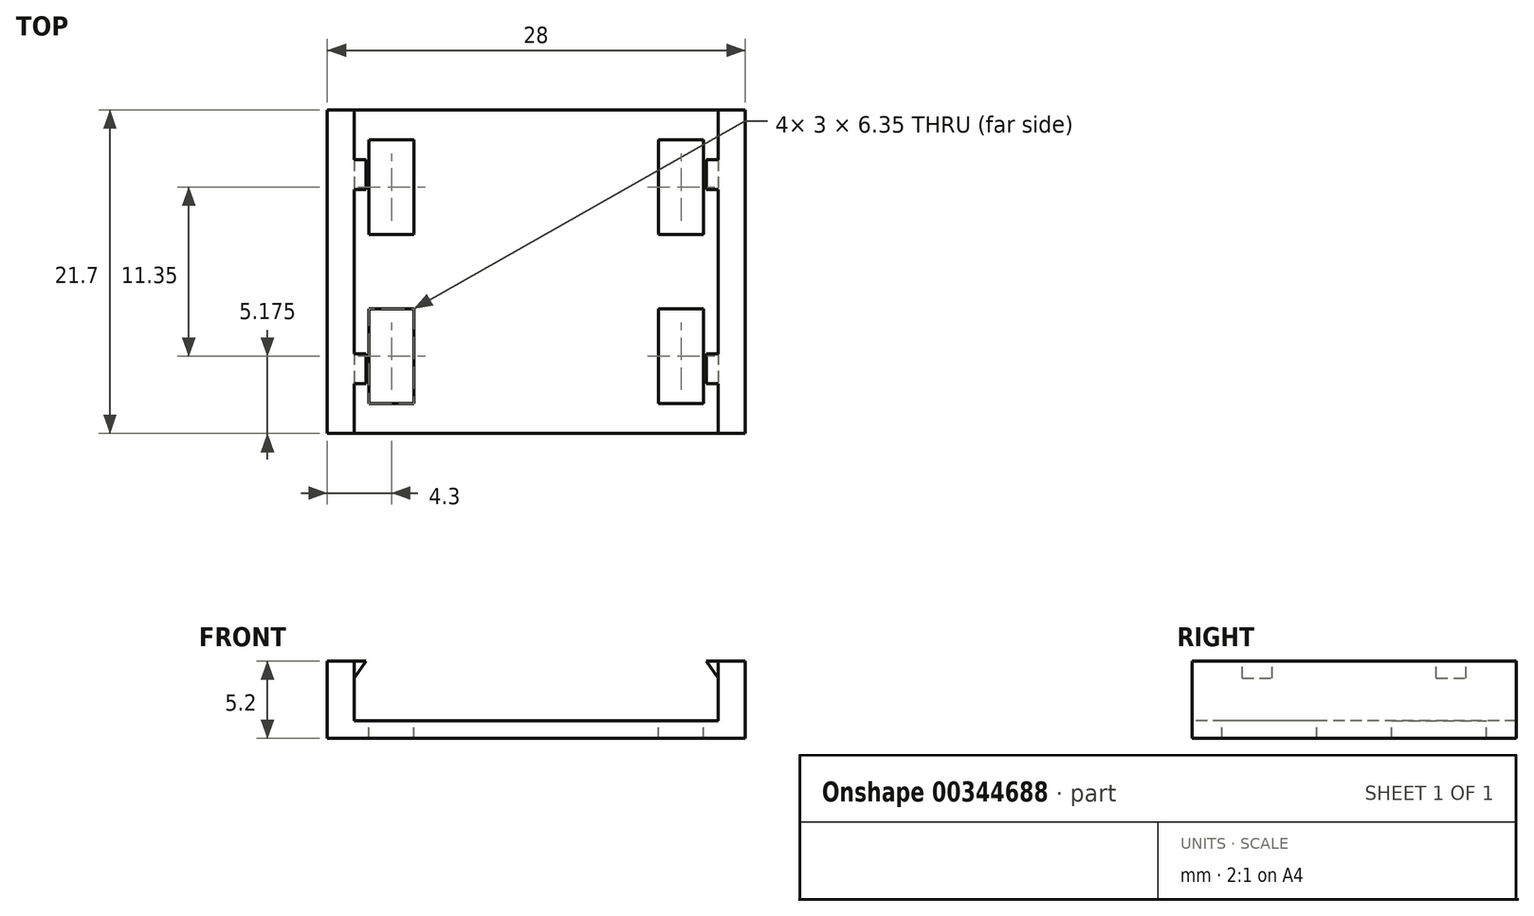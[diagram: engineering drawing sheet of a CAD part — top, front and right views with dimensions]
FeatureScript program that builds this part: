
annotation { "Feature Type Name" : "Feature", "Feature Type Description" : "" }
export const myFeature = defineFeature(function(context is Context, id is Id, definition is map)
    precondition{}
    {
        {
            var Q0;
            Q0=qCreatedBy(makeId("Top.planeOp"),FACE);
            var sketch = newSketch(context, id + "F0", { "sketchPlane" : qUnion([Q0])});
            skLineSegment(sketch, "E0.bottom", {"start": v(-14, 16.35) * mm, "end": v(14, 16.35) * mm});
            skLineSegment(sketch, "E0.top", {"start": v(-14, -16.35) * mm, "end": v(14, -16.35) * mm});
            skLineSegment(sketch, "E0.left", {"start": v(-14, 16.35) * mm, "end": v(-14, -16.35) * mm});
            skLineSegment(sketch, "E0.right", {"start": v(14, 16.35) * mm, "end": v(14, -16.35) * mm});
            skPoint(sketch, "E0.middle", {"position": v(0, 0) * mm});
            skSolve(sketch);
        }
        {
            var Q0;
            Q0=makeQuery(id+"F0.imprint","IMPRINT",FACE,{"disambiguationData":[TD([[makeQuery(id+"F0.imprint","IMPRINT",EDGE,{"derivedFrom":sQuery(id+"F0.wireOp",EDGE,"E0.bottom")}),-1.0]])]});
            extrude(context, id + "F1", {"entities" : qUnion([Q0]), "depth" : 1.2 * mm});
        }
        {
            var Q0;
            {var subQ5=sQuery(id+"F0.wireOp",EDGE,"E0.right");var subQ6=sQuery(id+"F0.wireOp",EDGE,"E0.left");var subQ7=sQuery(id+"F0.wireOp",EDGE,"E0.top");var subQ8=sQuery(id+"F0.wireOp",EDGE,"E0.bottom");var subQ9=makeQuery(id+"F1.opExtrude","CAP_FACE",FACE,{"disambiguationData":[OSD([subQ8,subQ7,subQ6,subQ5])],"isStart":false});var subQ12=subQ9;Q0=makeQuery(id+"FTskU3KK5imesQs_1.opFillet","MERGE",FACE,{"derivedFrom":[makeQuery(id+"FZi3CJKkktuihJ1_1.boolean.opBoolean","SPLIT",FACE,{"disambiguationData":[TD([makeQuery(id+"F1.opExtrude","SWEPT_FACE",FACE,{"disambiguationData":[OSD([subQ8])]})])],"derivedFrom":subQ12}),makeQuery(id+"FZ7EBSF1tdb4njM_1.boolean.opBoolean","MERGE",FACE,{"derivedFrom":[makeQuery(id+"FZi3CJKkktuihJ1_1.boolean.opBoolean","SPLIT",FACE,{"disambiguationData":[TD([makeQuery(id+"FlsG0jWeIkAughT_1.opExtrude","SWEPT_FACE",FACE,{"disambiguationData":[OSD([sQuery(id+"F5Wyuop6bpOGen8_1.wireOp",EDGE,"vaNtV44L-idVL-UOBQ-HHhe-vYpkaX2QMto8.bottom")])]})])],"derivedFrom":subQ12}),makeQuery(id+"FZ7EBSF1tdb4njM_1.opExtrude","CAP_FACE",FACE,{"disambiguationData":[OSD([sQuery(id+"FoSm93bD1NxVTFu_1.wireOp",EDGE,"97a7e462-43fe-4127-a601-1d90c2ab95a00.MirrorCS"),sQuery(id+"FoSm93bD1NxVTFu_1.wireOp",EDGE,"97a7e462-43fe-4127-a601-1d90c2ab95a01.MirrorCS"),sQuery(id+"FoSm93bD1NxVTFu_1.wireOp",EDGE,"97a7e462-43fe-4127-a601-1d90c2ab95a02.MirrorCS"),sQuery(id+"FoSm93bD1NxVTFu_1.wireOp",EDGE,"97a7e462-43fe-4127-a601-1d90c2ab95a03.MirrorCS")])],"isStart":false})]}),makeQuery(id+"FZ7EBSF1tdb4njM_1.boolean.opBoolean","MERGE",FACE,{"derivedFrom":[makeQuery(id+"FZi3CJKkktuihJ1_1.boolean.opBoolean","SPLIT",FACE,{"disambiguationData":[TD([makeQuery(id+"FlsG0jWeIkAughT_1.opExtrude","SWEPT_FACE",FACE,{"disambiguationData":[OSD([sQuery(id+"F5Wyuop6bpOGen8_1.wireOp",EDGE,"5b2c8ccd-c1e1-48dd-aecc-73c440124aab0.MirrorCS")])]})])],"derivedFrom":subQ12}),makeQuery(id+"FZ7EBSF1tdb4njM_1.opExtrude","CAP_FACE",FACE,{"disambiguationData":[OSD([sQuery(id+"FoSm93bD1NxVTFu_1.wireOp",EDGE,"85c03d27-702a-4580-8be8-e1d3315b53173.MirrorCS"),sQuery(id+"FoSm93bD1NxVTFu_1.wireOp",EDGE,"85c03d27-702a-4580-8be8-e1d3315b53174.MirrorCS"),sQuery(id+"FoSm93bD1NxVTFu_1.wireOp",EDGE,"85c03d27-702a-4580-8be8-e1d3315b53176.MirrorCS"),sQuery(id+"FoSm93bD1NxVTFu_1.wireOp",EDGE,"85c03d27-702a-4580-8be8-e1d3315b53177.MirrorCS")])],"isStart":false})]})]});}
            var sketch = newSketch(context, id + "F2", { "sketchPlane" : qUnion([Q0])});
            skLineSegment(sketch, "E1.bottom", {"start": v(-12.2, 15.35) * mm, "end": v(12.2, 15.35) * mm});
            skLineSegment(sketch, "E1.top", {"start": v(-12.2, -15.35) * mm, "end": v(12.2, -15.35) * mm});
            skLineSegment(sketch, "E1.left", {"start": v(-12.2, 15.35) * mm, "end": v(-12.2, -15.35) * mm});
            skLineSegment(sketch, "E1.right", {"start": v(12.2, 15.35) * mm, "end": v(12.2, -15.35) * mm});
            skPoint(sketch, "E1.middle", {"position": v(0, 0) * mm});
            skSolve(sketch);
        }
        {
            var Q0;
            Q0=makeQuery(id+"F2.imprint","IMPRINT",FACE,{"disambiguationData":[TD([[makeQuery(id+"F2.imprint","IMPRINT",EDGE,{"derivedFrom":sQuery(id+"F2.wireOp",EDGE,"E1.bottom")}),1.0]])]});
            extrude(context, id + "F3", {"entities" : qUnion([Q0]), "operationType" : NewBodyOperationType.ADD, "depth" : 4 * mm});
        }
        {
            var Q0;
            Q0=makeQuery(id+"F3.opExtrude","CAP_FACE",FACE,{"disambiguationData":[OSD([sQuery(id+"F0.wireOp",EDGE,"E0.bottom"),sQuery(id+"F0.wireOp",EDGE,"E0.top"),sQuery(id+"F0.wireOp",EDGE,"E0.left"),sQuery(id+"F0.wireOp",EDGE,"E0.right"),sQuery(id+"F2.wireOp",EDGE,"E1.bottom"),sQuery(id+"F2.wireOp",EDGE,"E1.top"),sQuery(id+"F2.wireOp",EDGE,"E1.left"),sQuery(id+"F2.wireOp",EDGE,"E1.right")])],"isStart":false});
            var sketch = newSketch(context, id + "F4", { "sketchPlane" : qUnion([Q0])});
            skLineSegment(sketch, "E2.bottom", {"start": v(-14, -16.35) * mm, "end": v(14, -16.35) * mm});
            skLineSegment(sketch, "E2.top", {"start": v(-14, -10.85) * mm, "end": v(14, -10.85) * mm});
            skLineSegment(sketch, "E2.left", {"start": v(-14, -16.35) * mm, "end": v(-14, -10.85) * mm});
            skLineSegment(sketch, "E2.right", {"start": v(14, -16.35) * mm, "end": v(14, -10.85) * mm});
            skLineSegment(sketch, "E3.MirrorCS", {"start": v(14, 16.35) * mm, "end": v(14, 10.85) * mm});
            skLineSegment(sketch, "E4.MirrorCS", {"start": v(-14, 16.35) * mm, "end": v(-14, 10.85) * mm});
            skLineSegment(sketch, "E5.MirrorCS", {"start": v(-14, 16.35) * mm, "end": v(14, 16.35) * mm});
            skLineSegment(sketch, "E6.MirrorCS", {"start": v(-14, 10.85) * mm, "end": v(14, 10.85) * mm});
            skSolve(sketch);
        }
        {
            var Q0;
            Q0 = qSketchRegion(id + "F4", true);
            extrude(context, id + "F5", {"entities" : qUnion([Q0]), "operationType" : NewBodyOperationType.REMOVE, "endBound" : BoundingType.THROUGH_ALL, "oppositeDirection" : true, "depth" : 25 * mm});
        }
        {
            var Q0;
            {var subQ5=sQuery(id+"F0.wireOp",EDGE,"E0.right");var subQ6=sQuery(id+"F0.wireOp",EDGE,"E0.left");var subQ7=sQuery(id+"F0.wireOp",EDGE,"E0.top");var subQ8=sQuery(id+"F0.wireOp",EDGE,"E0.bottom");var subQ9=makeQuery(id+"F1.opExtrude","CAP_FACE",FACE,{"disambiguationData":[OSD([subQ8,subQ7,subQ6,subQ5])],"isStart":false});var subQ12=subQ9;Q0=makeQuery(id+"FTskU3KK5imesQs_1.opFillet","MERGE",FACE,{"derivedFrom":[makeQuery(id+"FZi3CJKkktuihJ1_1.boolean.opBoolean","SPLIT",FACE,{"disambiguationData":[TD([makeQuery(id+"F1.opExtrude","SWEPT_FACE",FACE,{"disambiguationData":[OSD([subQ8])]})])],"derivedFrom":subQ12}),makeQuery(id+"FZ7EBSF1tdb4njM_1.boolean.opBoolean","MERGE",FACE,{"derivedFrom":[makeQuery(id+"FZi3CJKkktuihJ1_1.boolean.opBoolean","SPLIT",FACE,{"disambiguationData":[TD([makeQuery(id+"FlsG0jWeIkAughT_1.opExtrude","SWEPT_FACE",FACE,{"disambiguationData":[OSD([sQuery(id+"F5Wyuop6bpOGen8_1.wireOp",EDGE,"vaNtV44L-idVL-UOBQ-HHhe-vYpkaX2QMto8.bottom")])]})])],"derivedFrom":subQ12}),makeQuery(id+"FZ7EBSF1tdb4njM_1.opExtrude","CAP_FACE",FACE,{"disambiguationData":[OSD([sQuery(id+"FoSm93bD1NxVTFu_1.wireOp",EDGE,"97a7e462-43fe-4127-a601-1d90c2ab95a00.MirrorCS"),sQuery(id+"FoSm93bD1NxVTFu_1.wireOp",EDGE,"97a7e462-43fe-4127-a601-1d90c2ab95a01.MirrorCS"),sQuery(id+"FoSm93bD1NxVTFu_1.wireOp",EDGE,"97a7e462-43fe-4127-a601-1d90c2ab95a02.MirrorCS"),sQuery(id+"FoSm93bD1NxVTFu_1.wireOp",EDGE,"97a7e462-43fe-4127-a601-1d90c2ab95a03.MirrorCS")])],"isStart":false})]}),makeQuery(id+"FZ7EBSF1tdb4njM_1.boolean.opBoolean","MERGE",FACE,{"derivedFrom":[makeQuery(id+"FZi3CJKkktuihJ1_1.boolean.opBoolean","SPLIT",FACE,{"disambiguationData":[TD([makeQuery(id+"FlsG0jWeIkAughT_1.opExtrude","SWEPT_FACE",FACE,{"disambiguationData":[OSD([sQuery(id+"F5Wyuop6bpOGen8_1.wireOp",EDGE,"5b2c8ccd-c1e1-48dd-aecc-73c440124aab0.MirrorCS")])]})])],"derivedFrom":subQ12}),makeQuery(id+"FZ7EBSF1tdb4njM_1.opExtrude","CAP_FACE",FACE,{"disambiguationData":[OSD([sQuery(id+"FoSm93bD1NxVTFu_1.wireOp",EDGE,"85c03d27-702a-4580-8be8-e1d3315b53173.MirrorCS"),sQuery(id+"FoSm93bD1NxVTFu_1.wireOp",EDGE,"85c03d27-702a-4580-8be8-e1d3315b53174.MirrorCS"),sQuery(id+"FoSm93bD1NxVTFu_1.wireOp",EDGE,"85c03d27-702a-4580-8be8-e1d3315b53176.MirrorCS"),sQuery(id+"FoSm93bD1NxVTFu_1.wireOp",EDGE,"85c03d27-702a-4580-8be8-e1d3315b53177.MirrorCS")])],"isStart":false})]})]});}
            var sketch = newSketch(context, id + "F6", { "sketchPlane" : qUnion([Q0])});
            skLineSegment(sketch, "E7.bottom", {"start": v(-12.2, -5.25) * mm, "end": v(-10.2, -5.25) * mm});
            skLineSegment(sketch, "E7.top", {"start": v(-12.2, 5.25) * mm, "end": v(-10.2, 5.25) * mm});
            skLineSegment(sketch, "E7.left", {"start": v(-12.2, -5.25) * mm, "end": v(-12.2, 5.25) * mm});
            skLineSegment(sketch, "E7.right", {"start": v(12.2, -5.25) * mm, "end": v(12.2, 5.25) * mm});
            skLineSegment(sketch, "E8.bottom", {"start": v(-12.2, -7.25) * mm, "end": v(-10.2, -7.25) * mm});
            skLineSegment(sketch, "E8.top", {"start": v(-12.2, -10.85) * mm, "end": v(-10.2, -10.85) * mm});
            skLineSegment(sketch, "E8.left", {"start": v(-12.2, -7.25) * mm, "end": v(-12.2, -10.85) * mm});
            skLineSegment(sketch, "E8.right", {"start": v(12.2, -7.25) * mm, "end": v(12.2, -10.85) * mm});
            skLineSegment(sketch, "E9.MirrorCS", {"start": v(-12.2, 7.25) * mm, "end": v(-10.2, 7.25) * mm});
            skLineSegment(sketch, "E10.MirrorCS", {"start": v(-12.2, 10.85) * mm, "end": v(12.2, 10.85) * mm});
            skLineSegment(sketch, "E11.MirrorCS", {"start": v(12.2, 7.25) * mm, "end": v(12.2, 10.85) * mm});
            skLineSegment(sketch, "E12.MirrorCS", {"start": v(-12.2, 7.25) * mm, "end": v(-12.2, 10.85) * mm});
            skLineSegment(sketch, "E13", {"start": v(-10.2, -10.85) * mm, "end": v(-10.2, -7.25) * mm});
            skLineSegment(sketch, "E14.MirrorCS", {"start": v(10.2, -10.85) * mm, "end": v(10.2, -7.25) * mm});
            skLineSegment(sketch, "E15.trimOffspring", {"start": v(-10.2, -5.25) * mm, "end": v(-10.2, 5.25) * mm});
            skLineSegment(sketch, "E16.trimOffspring", {"start": v(10.2, -7.25) * mm, "end": v(12.2, -7.25) * mm});
            skLineSegment(sketch, "E17.trimOffspring", {"start": v(10.2, -10.85) * mm, "end": v(12.2, -10.85) * mm});
            skLineSegment(sketch, "E18.trimOffspring", {"start": v(10.2, -5.25) * mm, "end": v(12.2, -5.25) * mm});
            skLineSegment(sketch, "E19.trimOffspring", {"start": v(10.2, 5.25) * mm, "end": v(12.2, 5.25) * mm});
            skLineSegment(sketch, "E20.trimOffspring", {"start": v(10.2, 7.25) * mm, "end": v(12.2, 7.25) * mm});
            skLineSegment(sketch, "E21.trimOffspring", {"start": v(-10.2, 7.25) * mm, "end": v(-10.2, 10.85) * mm});
            skLineSegment(sketch, "E22.trimOffspring", {"start": v(10.2, -5.25) * mm, "end": v(10.2, 5.25) * mm});
            skLineSegment(sketch, "E23.trimOffspring", {"start": v(10.2, 7.25) * mm, "end": v(10.2, 10.85) * mm});
            skSolve(sketch);
        }
        {
            var Q0;
            Q0=makeQuery(id+"F6.imprint","IMPRINT",FACE,{"disambiguationData":[TD([[makeQuery(id+"F6.imprint","IMPRINT",EDGE,{"derivedFrom":sQuery(id+"F6.wireOp",EDGE,"E8.bottom")}),-1.0]])]});
            var Q1;
            Q1=makeQuery(id+"F6.imprint","IMPRINT",FACE,{"disambiguationData":[TD([[makeQuery(id+"F6.imprint","IMPRINT",EDGE,{"derivedFrom":sQuery(id+"F6.wireOp",EDGE,"E7.bottom")}),1.0]])]});
            var Q2;
            Q2=makeQuery(id+"F6.imprint","IMPRINT",FACE,{"disambiguationData":[TD([[makeQuery(id+"F6.imprint","IMPRINT",EDGE,{"derivedFrom":sQuery(id+"F6.wireOp",EDGE,"E9.MirrorCS")}),1.0]])]});
            var Q3;
            Q3=makeQuery(id+"F6.imprint","IMPRINT",FACE,{"disambiguationData":[TD([[makeQuery(id+"F6.imprint","IMPRINT",EDGE,{"derivedFrom":sQuery(id+"F6.wireOp",EDGE,"E8.right")}),-1.0]])]});
            var Q4;
            Q4=makeQuery(id+"F6.imprint","IMPRINT",FACE,{"disambiguationData":[TD([[makeQuery(id+"F6.imprint","IMPRINT",EDGE,{"derivedFrom":sQuery(id+"F6.wireOp",EDGE,"E7.right")}),-1.0]])]});
            var Q5;
            {var subQ0=sQuery(id+"F6.wireOp",EDGE,"E11.MirrorCS");Q5=makeQuery(id+"F6.imprint","IMPRINT",FACE,{"disambiguationData":[TD([[makeQuery(id+"F6.imprint","IMPRINT",EDGE,{"derivedFrom":subQ0}),-1.0]])]});}
            extrude(context, id + "F7", {"entities" : qUnion([Q0, Q1, Q2, Q3, Q4, Q5]), "operationType" : NewBodyOperationType.REMOVE, "depth" : 30 * mm});
        }
        {
            var Q0;
            Q0=makeQuery(id+"F5.boolean.opBoolean","COPY",FACE,{"derivedFrom":makeQuery(id+"F5.opExtrude","SWEPT_FACE",FACE,{"disambiguationData":[OSD([sQuery(id+"F4.wireOp",EDGE,"E6.MirrorCS")])]})});
            var sketch = newSketch(context, id + "F8", { "sketchPlane" : qUnion([Q0])});
            skLineSegment(sketch, "E24", {"start": v(-12.2, 5.2) * mm, "end": v(-11.4, 5.2) * mm});
            skLineSegment(sketch, "E25", {"start": v(-11.4, 5.2) * mm, "end": v(-12.2, 4.06) * mm});
            skLineSegment(sketch, "E26", {"start": v(-12.2, 4.06) * mm, "end": v(-12.2, 5.2) * mm});
            skLineSegment(sketch, "E27.MirrorCS", {"start": v(12.2, 5.2) * mm, "end": v(11.4, 5.2) * mm});
            skLineSegment(sketch, "E28.MirrorCS", {"start": v(11.4, 5.2) * mm, "end": v(12.2, 4.06) * mm});
            skLineSegment(sketch, "E29.MirrorCS", {"start": v(12.2, 4.06) * mm, "end": v(12.2, 5.2) * mm});
            skSolve(sketch);
        }
        {
            var Q0;
            Q0=makeQuery(id+"F8.imprint","IMPRINT",FACE,{"disambiguationData":[TD([[makeQuery(id+"F8.imprint","IMPRINT",EDGE,{"derivedFrom":sQuery(id+"F8.wireOp",EDGE,"E24")}),-1.0]])]});
            var Q1;
            Q1=makeQuery(id+"F8.imprint","IMPRINT",FACE,{"disambiguationData":[TD([[makeQuery(id+"F8.imprint","IMPRINT",EDGE,{"derivedFrom":sQuery(id+"F8.wireOp",EDGE,"E27.MirrorCS")}),1.0]])]});
            var Q2;
            Q2=makeQuery(id+"F5.boolean.opBoolean","COPY",FACE,{"derivedFrom":makeQuery(id+"F5.opExtrude","SWEPT_FACE",FACE,{"disambiguationData":[OSD([sQuery(id+"F4.wireOp",EDGE,"E2.top")])]})});
            extrude(context, id + "F9", {"entities" : qUnion([Q0, Q1]), "operationType" : NewBodyOperationType.ADD, "endBound" : BoundingType.UP_TO_SURFACE, "oppositeDirection" : true, "endBoundEntityFace" : qUnion([Q2]), "depth" : 25 * mm});
        }
        {
            var Q0;
            {var subQ0=sQuery(id+"F0.wireOp",EDGE,"E0.right");var subQ1=sQuery(id+"F2.wireOp",EDGE,"E1.right");Q0=makeQuery(id+"F9.boolean.opBoolean","MERGE",FACE,{"derivedFrom":[makeQuery(id+"F5.boolean.opBoolean","SPLIT",FACE,{"disambiguationData":[TD([makeQuery(id+"F1.opExtrude","SWEPT_FACE",FACE,{"disambiguationData":[OSD([subQ0])]})])],"derivedFrom":makeQuery(id+"F3.opExtrude","CAP_FACE",FACE,{"disambiguationData":[OSD([sQuery(id+"F0.wireOp",EDGE,"E0.bottom"),sQuery(id+"F0.wireOp",EDGE,"E0.top"),sQuery(id+"F0.wireOp",EDGE,"E0.left"),subQ0,sQuery(id+"F2.wireOp",EDGE,"E1.bottom"),sQuery(id+"F2.wireOp",EDGE,"E1.top"),sQuery(id+"F2.wireOp",EDGE,"E1.left"),subQ1])],"isStart":false})}),makeQuery(id+"F9.opExtrude","SWEPT_FACE",FACE,{"disambiguationData":[OSD([sQuery(id+"F8.wireOp",EDGE,"E24")])]})]});}
            var sketch = newSketch(context, id + "F10", { "sketchPlane" : qUnion([Q0])});
            skLineSegment(sketch, "E30.bottom", {"start": v(12.2, 5.5) * mm, "end": v(-12.2, 5.5) * mm});
            skLineSegment(sketch, "E30.top", {"start": v(12.2, -5.5) * mm, "end": v(-12.2, -5.5) * mm});
            skLineSegment(sketch, "E30.left", {"start": v(12.2, 5.5) * mm, "end": v(12.2, -5.5) * mm});
            skLineSegment(sketch, "E30.right", {"start": v(-12.2, 5.5) * mm, "end": v(-12.2, -5.5) * mm});
            skPoint(sketch, "E30.middle", {"position": v(0, 0) * mm});
            skLineSegment(sketch, "E31.bottom", {"start": v(12.2, 10.85) * mm, "end": v(-12.2, 10.85) * mm});
            skLineSegment(sketch, "E31.top", {"start": v(12.2, 7.5) * mm, "end": v(-12.2, 7.5) * mm});
            skLineSegment(sketch, "E31.left", {"start": v(12.2, 10.85) * mm, "end": v(12.2, 7.5) * mm});
            skLineSegment(sketch, "E31.right", {"start": v(-12.2, 10.85) * mm, "end": v(-12.2, 7.5) * mm});
            skPoint(sketch, "E31.middle", {"position": v(0, 9.18) * mm});
            skLineSegment(sketch, "E32.MirrorCS", {"start": v(12.2, -7.5) * mm, "end": v(-12.2, -7.5) * mm});
            skLineSegment(sketch, "E33.MirrorCS", {"start": v(12.2, -10.85) * mm, "end": v(12.2, -7.5) * mm});
            skLineSegment(sketch, "E34.MirrorCS", {"start": v(-12.2, -10.85) * mm, "end": v(-12.2, -7.5) * mm});
            skPoint(sketch, "E35.MirrorP", {"position": v(0, -9.18) * mm});
            skLineSegment(sketch, "E36.MirrorCS", {"start": v(12.2, -10.85) * mm, "end": v(-12.2, -10.85) * mm});
            skSolve(sketch);
        }
        {
            var Q0;
            Q0 = qSketchRegion(id + "F10", true);
            extrude(context, id + "F11", {"entities" : qUnion([Q0]), "operationType" : NewBodyOperationType.REMOVE, "oppositeDirection" : true, "depth" : 3 * mm});
        }
        {
            var Q0;
            Q0=makeQuery(id+"F1.opExtrude","CAP_FACE",FACE,{"disambiguationData":[OSD([sQuery(id+"F0.wireOp",EDGE,"E0.bottom"),sQuery(id+"F0.wireOp",EDGE,"E0.top"),sQuery(id+"F0.wireOp",EDGE,"E0.left"),sQuery(id+"F0.wireOp",EDGE,"E0.right")])],"isStart":false});
            var sketch = newSketch(context, id + "F12", { "sketchPlane" : qUnion([Q0])});
            skLineSegment(sketch, "E37.bottom", {"start": v(-8.2, 2.5) * mm, "end": v(-11.2, 2.5) * mm});
            skLineSegment(sketch, "E37.top", {"start": v(-8.2, 8.85) * mm, "end": v(-11.2, 8.85) * mm});
            skLineSegment(sketch, "E37.left", {"start": v(-8.2, 2.5) * mm, "end": v(-8.2, 8.85) * mm});
            skLineSegment(sketch, "E37.right", {"start": v(-11.2, 2.5) * mm, "end": v(-11.2, 8.85) * mm});
            skPoint(sketch, "E37.middle", {"position": v(-9.7, 5.67) * mm});
            skLineSegment(sketch, "E38.MirrorCS", {"start": v(-8.2, -8.85) * mm, "end": v(-11.2, -8.85) * mm});
            skLineSegment(sketch, "E39.MirrorCS", {"start": v(-8.2, -2.5) * mm, "end": v(-11.2, -2.5) * mm});
            skLineSegment(sketch, "E40.MirrorCS", {"start": v(-8.2, -2.5) * mm, "end": v(-8.2, -8.85) * mm});
            skLineSegment(sketch, "E41.MirrorCS", {"start": v(-11.2, -2.5) * mm, "end": v(-11.2, -8.85) * mm});
            skPoint(sketch, "E42.MirrorP", {"position": v(-9.7, -5.67) * mm});
            skLineSegment(sketch, "E43.MirrorCS", {"start": v(8.2, -2.5) * mm, "end": v(11.2, -2.5) * mm});
            skPoint(sketch, "E44.MirrorP", {"position": v(9.7, 5.67) * mm});
            skLineSegment(sketch, "E45.MirrorCS", {"start": v(8.2, -8.85) * mm, "end": v(11.2, -8.85) * mm});
            skLineSegment(sketch, "E46.MirrorCS", {"start": v(8.2, 2.5) * mm, "end": v(11.2, 2.5) * mm});
            skLineSegment(sketch, "E47.MirrorCS", {"start": v(8.2, 8.85) * mm, "end": v(11.2, 8.85) * mm});
            skLineSegment(sketch, "E48.MirrorCS", {"start": v(11.2, -2.5) * mm, "end": v(11.2, -8.85) * mm});
            skLineSegment(sketch, "E49.MirrorCS", {"start": v(8.2, -2.5) * mm, "end": v(8.2, -8.85) * mm});
            skLineSegment(sketch, "E50.MirrorCS", {"start": v(11.2, 2.5) * mm, "end": v(11.2, 8.85) * mm});
            skLineSegment(sketch, "E51.MirrorCS", {"start": v(8.2, 2.5) * mm, "end": v(8.2, 8.85) * mm});
            skPoint(sketch, "E52.MirrorP", {"position": v(9.7, -5.67) * mm});
            skSolve(sketch);
        }
        {
            var Q0;
            Q0=makeQuery(id+"F12.imprint","IMPRINT",FACE,{"disambiguationData":[TD([[makeQuery(id+"F12.imprint","IMPRINT",EDGE,{"derivedFrom":sQuery(id+"F12.wireOp",EDGE,"E37.bottom")}),-1.0]])]});
            var Q1;
            Q1=makeQuery(id+"F12.imprint","IMPRINT",FACE,{"disambiguationData":[TD([[makeQuery(id+"F12.imprint","IMPRINT",EDGE,{"derivedFrom":sQuery(id+"F12.wireOp",EDGE,"E38.MirrorCS")}),-1.0]])]});
            var Q2;
            Q2=makeQuery(id+"F12.imprint","IMPRINT",FACE,{"disambiguationData":[TD([[makeQuery(id+"F12.imprint","IMPRINT",EDGE,{"derivedFrom":sQuery(id+"F12.wireOp",EDGE,"E46.MirrorCS")}),1.0]])]});
            var Q3;
            Q3=makeQuery(id+"F12.imprint","IMPRINT",FACE,{"disambiguationData":[TD([[makeQuery(id+"F12.imprint","IMPRINT",EDGE,{"derivedFrom":sQuery(id+"F12.wireOp",EDGE,"E43.MirrorCS")}),-1.0]])]});
            extrude(context, id + "F13", {"entities" : qUnion([Q0, Q1, Q2, Q3]), "operationType" : NewBodyOperationType.REMOVE, "oppositeDirection" : true, "depth" : 25 * mm});
        }
    });
